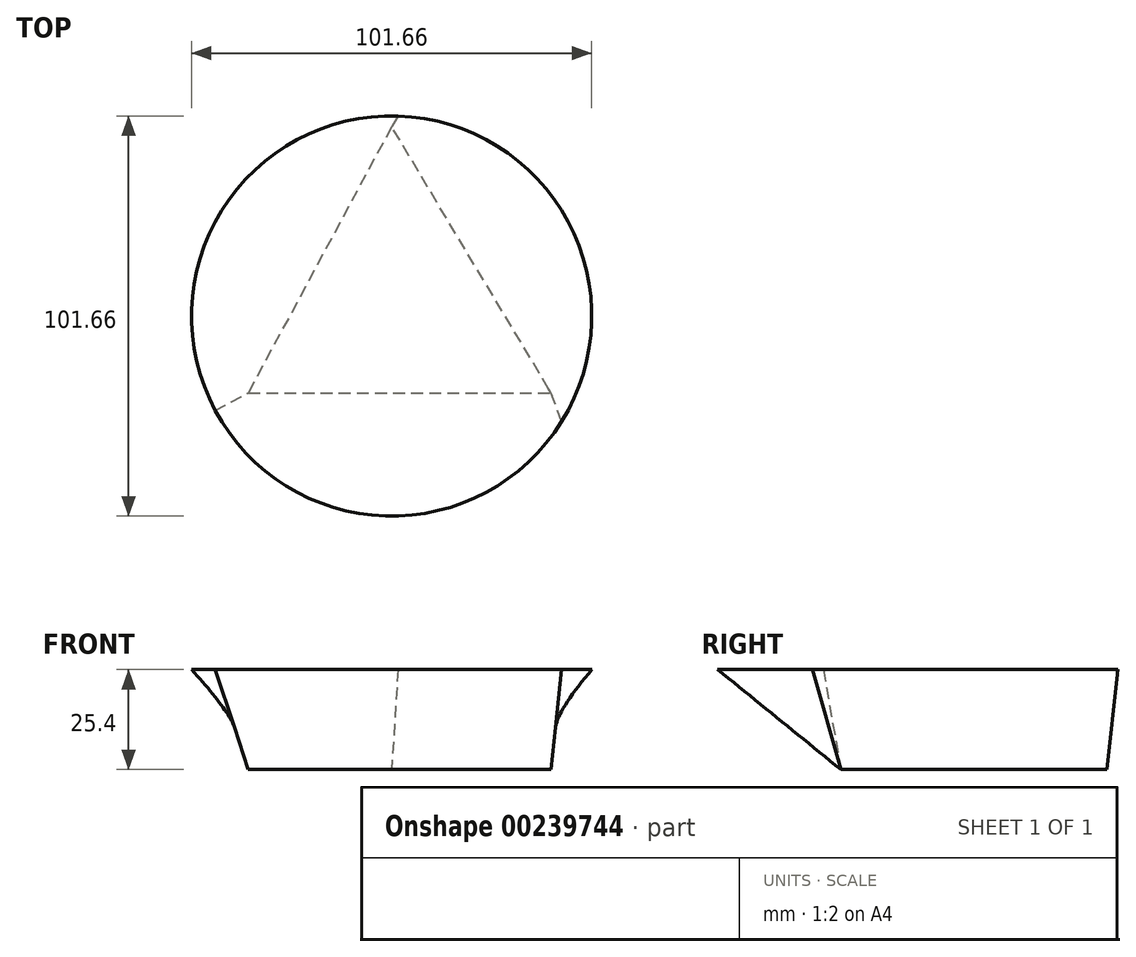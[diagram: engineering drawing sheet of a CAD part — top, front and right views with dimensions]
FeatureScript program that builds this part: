
annotation { "Feature Type Name" : "Feature", "Feature Type Description" : "" }
export const myFeature = defineFeature(function(context is Context, id is Id, definition is map)
    precondition{}
    {
        {
            var Q0;
            Q0=qCreatedBy(makeId("Top.planeOp"),FACE);
            var sketch = newSketch(context, id + "F0", { "sketchPlane" : qUnion([Q0])});
            skLineSegment(sketch, "E0", {"start": v(-36.43, -36.58) * mm, "end": v(40.52, -36.58) * mm});
            skLineSegment(sketch, "E1", {"start": v(40.52, -36.58) * mm, "end": v(0, 31.04) * mm});
            skLineSegment(sketch, "E2", {"start": v(0, 31.04) * mm, "end": v(-36.43, -36.58) * mm});
            skCircle(sketch, "E3", {"center": v(0, -16.18) * mm, "radius": 19.67 * mm, "construction": true});
            skSolve(sketch);
        }
        {
            var Q0;
            Q0=qCreatedBy(makeId("Top.planeOp"),FACE);
            cPlane(context, id + "F1", {"entities" : qUnion([Q0]), "cplaneType" : CPlaneType.OFFSET, "offset" : 25.4 * mm, "width" : 152.4 * mm, "height" : 152.4 * mm});
        }
        {
            var Q0;
            Q0=qCreatedBy(id+"F1.planeOp",FACE);
            var sketch = newSketch(context, id + "F2", { "sketchPlane" : qUnion([Q0])});
            skCircle(sketch, "E4", {"center": v(0, -17.05) * mm, "radius": 50.83 * mm});
            skSolve(sketch);
        }
        {
            var Q0;
            Q0 = qSketchRegion(id + "F2", true);
            var Q1;
            Q1 = qSketchRegion(id + "F0", true);
            loft(context, id + "F3", {"sheetProfilesArray" : [{ "sheetProfileEntities" : qUnion([Q0]) }, { "sheetProfileEntities" : qUnion([Q1]) }]});
        }
    });
